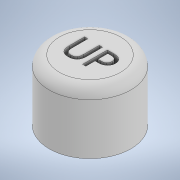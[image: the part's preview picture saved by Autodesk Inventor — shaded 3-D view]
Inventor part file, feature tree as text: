
AUTODESK INVENTOR PART (.ipt)
format: ipt  version: 2021 (Build 250183000, 183)  size: 168,448 bytes
history: native  units: mm
features: extrude x3, sketch x3, fillet x1
ambient origin geometry x8: Origin, YZ Plane, XZ Plane, XY Plane, X Axis, Y Axis, Z Axis, Center Point
bodies: Solid1 (feature_tree)
feature tree (7):
  extrude  "Extrusion1"  Depth=2.5mm TaperAngle=0.0deg
  fillet  "Fillet1"  Radius=2.5mm
  extrude  "Extrusion2"  Depth=2.5mm TaperAngle=0.0deg
  extrude  "Extrusion3"  [1 undecoded]
  sketch  "Sketch1"  dims[d0=20.0mm d1=15.0mm d2=0.0mm d3=2.5mm]
  sketch  "Sketch2"  dims[d4=5.0mm d5=0.0mm d6=2.5mm d7=0.0mm]
  sketch  "Sketch3"
note: 1 required parameter value undecoded (feature->parameter linkage not recoverable at this tier; creation-order binding heuristic only, values carry confidence <= 0.55)
